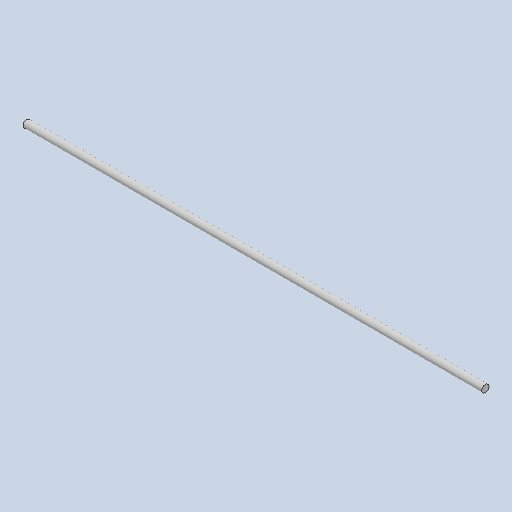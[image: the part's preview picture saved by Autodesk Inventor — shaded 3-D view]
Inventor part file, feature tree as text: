
AUTODESK INVENTOR PART (.ipt)
format: ipt  version: 2023 (Build 270158000, 158)  size: 80,384 bytes
history: native  units: mm
features: extrude x1, sketch x1
ambient origin geometry x8: Origin, YZ Plane, XZ Plane, XY Plane, X Axis, Y Axis, Z Axis, Center Point
bodies: Solid1 (feature_tree)
feature tree (2):
  extrude  "Extrusion1"  Depth=500.0mm TaperAngle=0.0deg
  sketch  "Sketch1"  dims[d0=8.0mm d1=500.0mm d2=0.0mm]
